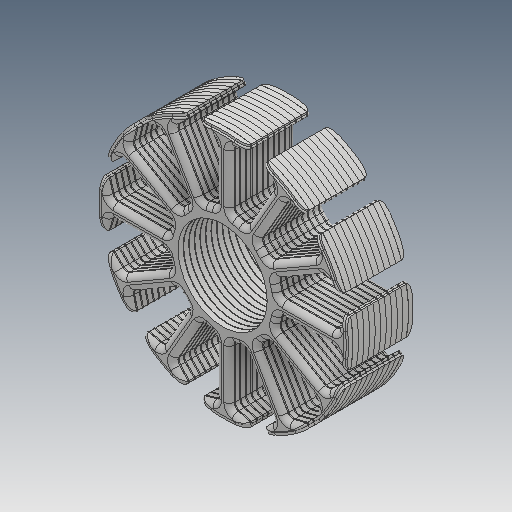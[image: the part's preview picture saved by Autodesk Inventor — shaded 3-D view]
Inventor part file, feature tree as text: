
AUTODESK INVENTOR PART (.ipt)
format: ipt  version: 2018 (Build 220112000, 112)  size: 7,859,712 bytes
history: native  units: mm
features: other x144, fillet x12
ambient origin geometry x8: Origin, YZ Plane, XZ Plane, XY Plane, X Axis, Y Axis, Z Axis, Center Point
bodies: Volumenkörper1 (feature_tree), Volumenkörper2 (feature_tree), Volumenkörper3 (feature_tree), Volumenkörper4 (feature_tree), Volumenkörper5 (feature_tree), Volumenkörper6 (feature_tree), Volumenkörper7 (feature_tree), Volumenkörper8 (feature_tree), Volumenkörper9 (feature_tree), Volumenkörper10 (feature_tree), Volumenkörper11 (feature_tree), Volumenkörper12 (feature_tree), Volumenkörper13 (feature_tree), Volumenkörper14 (feature_tree), Volumenkörper15 (feature_tree), Volumenkörper16 (feature_tree), Volumenkörper17 (feature_tree), Volumenkörper18 (feature_tree), Volumenkörper19 (feature_tree), Volumenkörper20 (feature_tree), Volumenkörper21 (feature_tree), Volumenkörper22 (feature_tree), Volumenkörper23 (feature_tree), Volumenkörper24 (feature_tree), Volumenkörper25 (feature_tree), Volumenkörper26 (feature_tree), Volumenkörper27 (feature_tree), Volumenkörper28 (feature_tree), Volumenkörper29 (feature_tree), Volumenkörper30 (feature_tree), Volumenkörper31 (feature_tree), Volumenkörper32 (feature_tree), Volumenkörper33 (feature_tree), Volumenkörper34 (feature_tree), Volumenkörper35 (feature_tree), Volumenkörper36 (feature_tree), Volumenkörper37 (feature_tree), Volumenkörper38 (feature_tree), Volumenkörper39 (feature_tree), Volumenkörper40 (feature_tree), Volumenkörper41 (feature_tree), Volumenkörper42 (feature_tree), Volumenkörper43 (feature_tree), Volumenkörper44 (feature_tree), Volumenkörper45 (feature_tree), Volumenkörper46 (feature_tree), Volumenkörper47 (feature_tree), Volumenkörper48 (feature_tree), Volumenkörper49 (feature_tree), Volumenkörper50 (feature_tree), Volumenkörper51 (feature_tree), Volumenkörper52 (feature_tree), Volumenkörper53 (feature_tree), Volumenkörper54 (feature_tree), Volumenkörper55 (feature_tree), Volumenkörper56 (feature_tree), Volumenkörper57 (feature_tree), Volumenkörper58 (feature_tree), Volumenkörper59 (feature_tree), Volumenkörper60 (feature_tree), Volumenkörper61 (feature_tree), Volumenkörper62 (feature_tree), Volumenkörper63 (feature_tree), Volumenkörper64 (feature_tree), Volumenkörper65 (feature_tree), Volumenkörper66 (feature_tree), Volumenkörper67 (feature_tree), Volumenkörper68 (feature_tree), Volumenkörper69 (feature_tree), Volumenkörper70 (feature_tree), Volumenkörper71 (feature_tree), Volumenkörper72 (feature_tree), Volumenkörper73 (feature_tree), Volumenkörper74 (feature_tree), Volumenkörper75 (feature_tree), Volumenkörper76 (feature_tree), Volumenkörper77 (feature_tree), Volumenkörper78 (feature_tree), Volumenkörper79 (feature_tree), Volumenkörper80 (feature_tree), Volumenkörper81 (feature_tree), Volumenkörper82 (feature_tree), Volumenkörper83 (feature_tree), Volumenkörper84 (feature_tree), Volumenkörper85 (feature_tree), Volumenkörper86 (feature_tree), Volumenkörper87 (feature_tree), Volumenkörper88 (feature_tree), Volumenkörper89 (feature_tree), Volumenkörper90 (feature_tree), Volumenkörper91 (feature_tree), Volumenkörper92 (feature_tree), Volumenkörper93 (feature_tree), Volumenkörper94 (feature_tree), Volumenkörper95 (feature_tree), Volumenkörper96 (feature_tree), Volumenkörper97 (feature_tree), Volumenkörper98 (feature_tree), Volumenkörper99 (feature_tree), Volumenkörper100 (feature_tree), Volumenkörper101 (feature_tree), Volumenkörper102 (feature_tree), Volumenkörper103 (feature_tree), Volumenkörper104 (feature_tree), Volumenkörper105 (feature_tree), Volumenkörper106 (feature_tree), Volumenkörper107 (feature_tree), Volumenkörper108 (feature_tree), Volumenkörper109 (feature_tree), Volumenkörper110 (feature_tree), Volumenkörper111 (feature_tree), Volumenkörper112 (feature_tree), Volumenkörper113 (feature_tree), Volumenkörper114 (feature_tree), Volumenkörper115 (feature_tree), Volumenkörper116 (feature_tree), Volumenkörper117 (feature_tree), Volumenkörper118 (feature_tree), Volumenkörper119 (feature_tree), Volumenkörper120 (feature_tree), Volumenkörper121 (feature_tree), Volumenkörper122 (feature_tree), Volumenkörper123 (feature_tree), Volumenkörper124 (feature_tree), Volumenkörper125 (feature_tree), Volumenkörper126 (feature_tree), Volumenkörper127 (feature_tree), Volumenkörper128 (feature_tree), Volumenkörper129 (feature_tree), Volumenkörper130 (feature_tree), Volumenkörper131 (feature_tree), Volumenkörper132 (feature_tree), Volumenkörper133 (feature_tree), Volumenkörper134 (feature_tree), Volumenkörper135 (feature_tree), Volumenkörper136 (feature_tree), Volumenkörper137 (feature_tree), Volumenkörper138 (feature_tree), Volumenkörper139 (feature_tree), Volumenkörper140 (feature_tree), Volumenkörper141 (feature_tree), Volumenkörper142 (feature_tree), Volumenkörper143 (feature_tree), Volumenkörper144 (feature_tree), Volumenkörper145 (feature_tree), Volumenkörper146 (feature_tree), Volumenkörper147 (feature_tree), Volumenkörper148 (feature_tree), Volumenkörper149 (feature_tree), Volumenkörper150 (feature_tree), Volumenkörper151 (feature_tree), Volumenkörper152 (feature_tree), Volumenkörper153 (feature_tree), Volumenkörper154 (feature_tree), Volumenkörper155 (feature_tree), Volumenkörper156 (feature_tree)
feature tree (156):
  other  "Split2[1]"
  other  "Split2[2]"
  other  "Split2[3]"
  other  "Split2[4]"
  other  "Split2[5]"
  other  "Split2[6]"
  other  "Split2[7]"
  other  "Split2[8]"
  other  "Split2[9]"
  other  "Split2[10]"
  other  "Split2[11]"
  other  "Split2[12]"
  other  "Split2[13]"
  other  "Split2[14]"
  other  "Split2[15]"
  other  "Split2[16]"
  other  "Split2[17]"
  other  "Split2[18]"
  other  "Split2[19]"
  other  "Split2[20]"
  other  "Split2[21]"
  other  "Split2[22]"
  other  "Split2[23]"
  other  "Split2[24]"
  other  "Split2[25]"
  other  "Split2[26]"
  other  "Split2[27]"
  other  "Split2[28]"
  other  "Split2[29]"
  other  "Split2[30]"
  other  "Split2[31]"
  other  "Split2[32]"
  other  "Split2[33]"
  other  "Split2[34]"
  other  "Split2[35]"
  other  "Split2[36]"
  other  "Split2[37]"
  other  "Split2[38]"
  other  "Split2[39]"
  other  "Split2[40]"
  other  "Split2[41]"
  other  "Split2[42]"
  other  "Split2[43]"
  other  "Split2[44]"
  other  "Split2[45]"
  other  "Split2[46]"
  other  "Split2[47]"
  other  "Split2[48]"
  other  "Split2[49]"
  other  "Split2[50]"
  other  "Split2[51]"
  other  "Split2[52]"
  other  "Split2[53]"
  other  "Split2[54]"
  other  "Split2[55]"
  other  "Split2[56]"
  other  "Split2[57]"
  other  "Split2[58]"
  other  "Split2[59]"
  other  "Split2[60]"
  other  "Split2[61]"
  other  "Split2[62]"
  other  "Split2[63]"
  other  "Split2[64]"
  other  "Split2[65]"
  other  "Split2[66]"
  other  "Split2[67]"
  other  "Split2[68]"
  other  "Split2[69]"
  other  "Split2[70]"
  other  "Split2[71]"
  other  "Split2[72]"
  other  "Split2[73]"
  other  "Split2[74]"
  other  "Split2[75]"
  other  "Split2[76]"
  other  "Split2[77]"
  other  "Split2[78]"
  other  "Split2[79]"
  other  "Split2[80]"
  other  "Split2[81]"
  other  "Split2[82]"
  other  "Split2[83]"
  other  "Split2[84]"
  other  "Split2[85]"
  other  "Split2[86]"
  other  "Split2[87]"
  other  "Split2[88]"
  other  "Split2[89]"
  other  "Split2[90]"
  other  "Split2[91]"
  other  "Split2[92]"
  other  "Split2[93]"
  other  "Split2[94]"
  other  "Split2[95]"
  other  "Split2[96]"
  other  "Split2[97]"
  other  "Split2[98]"
  other  "Split2[99]"
  other  "Split2[100]"
  other  "Split2[101]"
  other  "Split2[102]"
  other  "Split2[103]"
  other  "Split2[104]"
  other  "Split2[105]"
  other  "Split2[106]"
  other  "Split2[107]"
  other  "Split2[108]"
  other  "Split2[109]"
  other  "Split2[110]"
  other  "Split2[111]"
  other  "Split2[112]"
  other  "Split2[113]"
  other  "Split2[114]"
  other  "Split2[115]"
  other  "Split2[116]"
  other  "Split2[117]"
  other  "Split2[118]"
  other  "Split2[119]"
  other  "Split2[120]"
  other  "Split2[121]"
  other  "Split2[122]"
  other  "Split2[123]"
  other  "Split2[124]"
  other  "Split2[125]"
  other  "Split2[126]"
  other  "Split2[127]"
  other  "Split2[128]"
  other  "Split2[129]"
  other  "Split2[130]"
  other  "Split2[131]"
  other  "Split2[132]"
  fillet  "Fillet20"  [1 undecoded]
  fillet  "Fillet24"  [1 undecoded]
  fillet  "Fillet23"  [1 undecoded]
  fillet  "Fillet22"  [1 undecoded]
  fillet  "Fillet21"  [1 undecoded]
  fillet  "Fillet15"  [1 undecoded]
  fillet  "Fillet13"  [1 undecoded]
  fillet  "Fillet11"  [1 undecoded]
  fillet  "Fillet9"  [1 undecoded]
  fillet  "Fillet7"  [1 undecoded]
  fillet  "Fillet5"  [1 undecoded]
  fillet  "Fillet25"  [1 undecoded]
  other  "Split2[145]"
  other  "Split2[146]"
  other  "Split2[147]"
  other  "Split2[148]"
  other  "Split2[149]"
  other  "Split2[150]"
  other  "Split2[151]"
  other  "Split2[152]"
  other  "Split2[153]"
  other  "Split2[154]"
  other  "Split2[155]"
  other  "Split2[156]"
note: 12 required parameter values undecoded (feature->parameter linkage not recoverable at this tier; creation-order binding heuristic only, values carry confidence <= 0.55)
